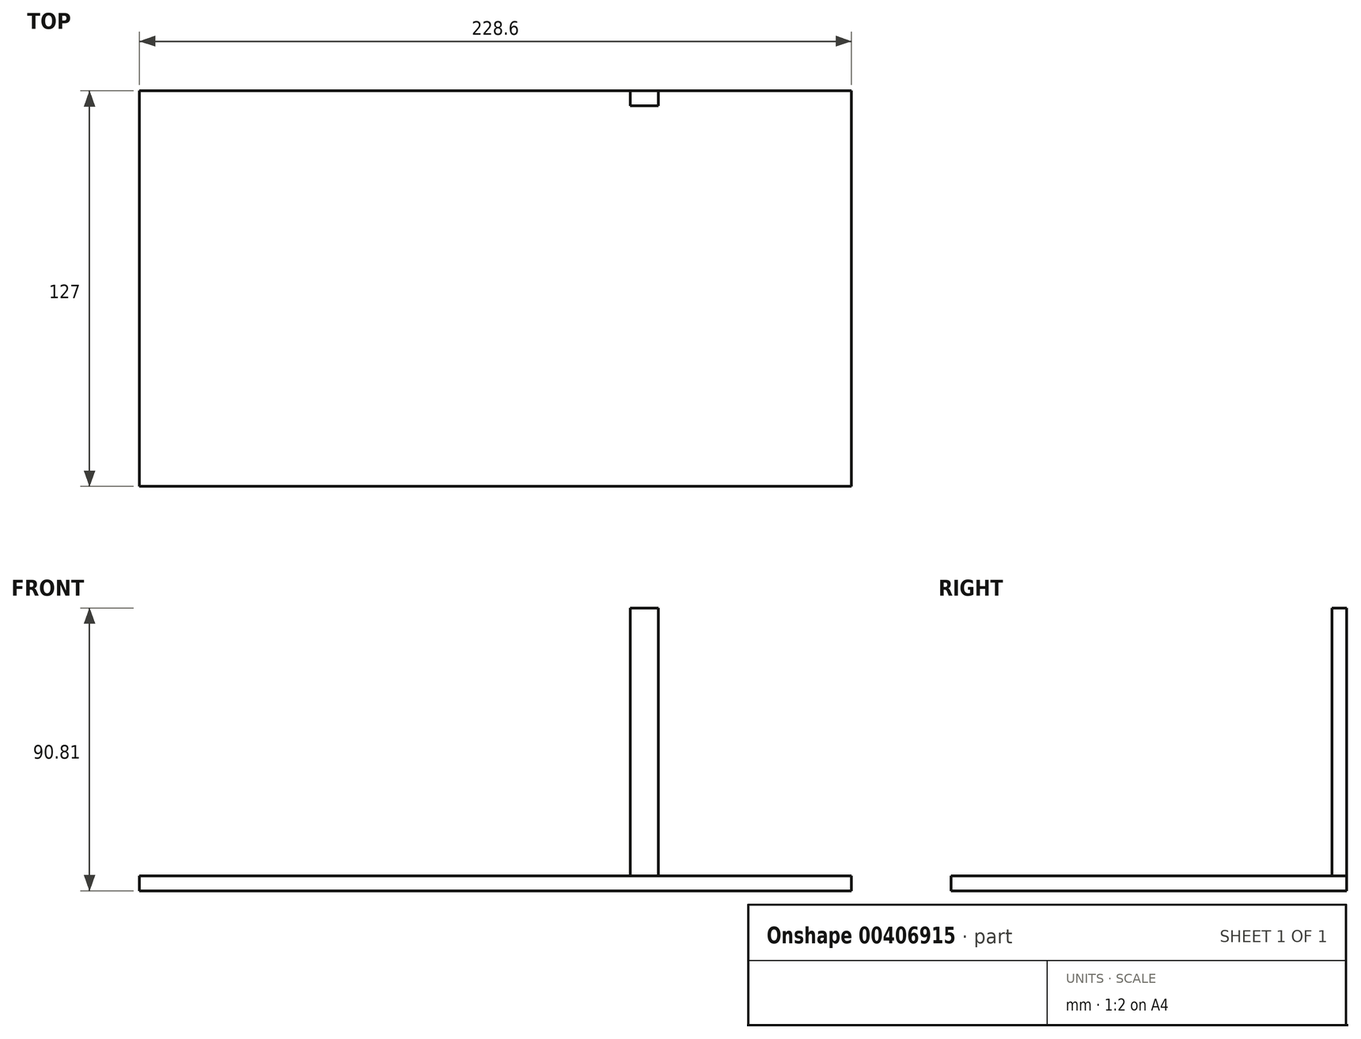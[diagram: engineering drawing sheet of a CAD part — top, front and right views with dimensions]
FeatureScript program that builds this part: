
annotation { "Feature Type Name" : "Feature", "Feature Type Description" : "" }
export const myFeature = defineFeature(function(context is Context, id is Id, definition is map)
    precondition{}
    {
        {
            var Q0;
            Q0=qCreatedBy(makeId("Front.planeOp"),FACE);
            var sketch = newSketch(context, id + "F0", { "sketchPlane" : qUnion([Q0])});
            skLineSegment(sketch, "E0", {"start": v(0, 0) * mm, "end": v(0, 86.03) * mm});
            skLineSegment(sketch, "E1", {"start": v(0, 86.03) * mm, "end": v(-9.07, 86.03) * mm});
            skLineSegment(sketch, "E2", {"start": v(-9.07, 86.03) * mm, "end": v(-9.07, 0) * mm});
            skLineSegment(sketch, "E3", {"start": v(-9.07, 0) * mm, "end": v(0, 0) * mm});
            skSolve(sketch);
        }
        {
            var Q0;
            Q0 = qSketchRegion(id + "F0", true);
            extrude(context, id + "F1", {"entities" : qUnion([Q0]), "depth" : 4.78 * mm});
        }
        {
            var Q0;
            Q0=makeQuery(id+"F1.opExtrude","SWEPT_FACE",FACE,{"disambiguationData":[OSD([sQuery(id+"F0.wireOp",EDGE,"E3")])]});
            var sketch = newSketch(context, id + "F2", { "sketchPlane" : qUnion([Q0])});
            skLineSegment(sketch, "E4.bottom", {"start": v(62, 0) * mm, "end": v(-166.6, 0) * mm});
            skLineSegment(sketch, "E4.top", {"start": v(62, 127) * mm, "end": v(-166.6, 127) * mm});
            skLineSegment(sketch, "E4.left", {"start": v(62, 0) * mm, "end": v(62, 127) * mm});
            skLineSegment(sketch, "E4.right", {"start": v(-166.6, 0) * mm, "end": v(-166.6, 127) * mm});
            skSolve(sketch);
        }
        {
            var Q0;
            Q0 = qSketchRegion(id + "F2", true);
            extrude(context, id + "F3", {"entities" : qUnion([Q0]), "operationType" : NewBodyOperationType.ADD, "depth" : 4.78 * mm});
        }
    });
